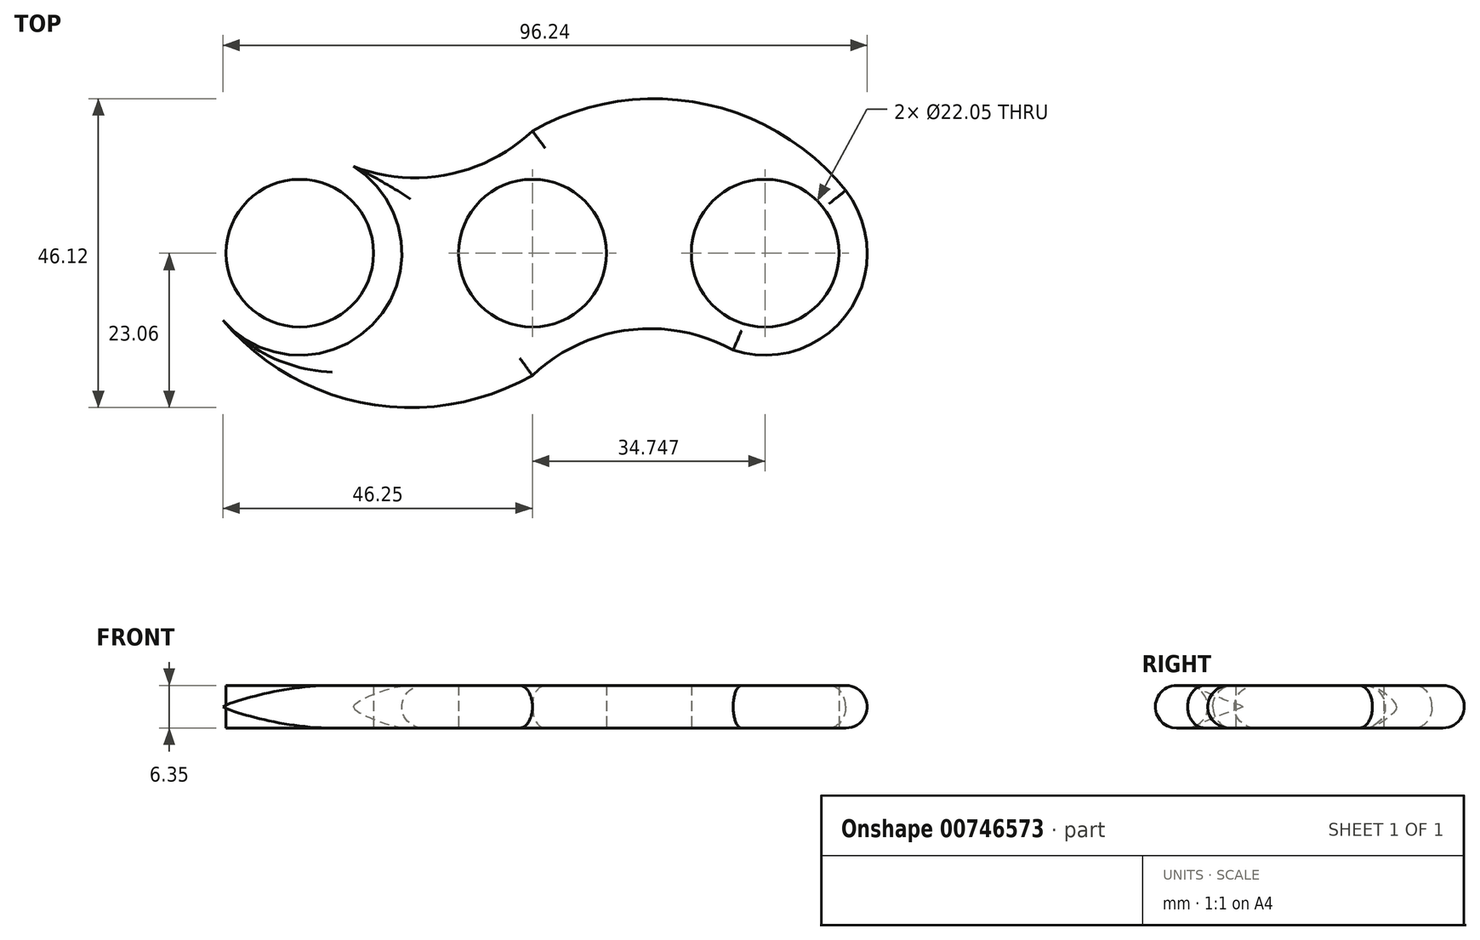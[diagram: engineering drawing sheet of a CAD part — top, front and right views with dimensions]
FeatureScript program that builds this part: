
annotation { "Feature Type Name" : "Feature", "Feature Type Description" : "" }
export const myFeature = defineFeature(function(context is Context, id is Id, definition is map)
    precondition{}
    {
        {
            var Q0;
            Q0=qCreatedBy(makeId("Top.planeOp"),FACE);
            var sketch = newSketch(context, id + "F0", { "sketchPlane" : qUnion([Q0])});
            skCircle(sketch, "E0", {"center": v(0, 0) * mm, "radius": 11.02 * mm});
            skCircle(sketch, "E1", {"center": v(34.75, 0) * mm, "radius": 11.02 * mm});
            skCircle(sketch, "E2.MirrorC", {"center": v(-34.75, 0) * mm, "radius": 11.02 * mm});
            skCircle(sketch, "E3", {"center": v(-34.75, 0) * mm, "radius": 15.24 * mm});
            skCircle(sketch, "E4.MirrorC", {"center": v(34.75, 0) * mm, "radius": 15.24 * mm});
            skArc(sketch, "E5", {"start": v(-29.97, 14.47) * mm, "mid": v(-14.37, 11.47) * mm, "end": v(0, 18.25) * mm});
            skArc(sketch, "E6", {"start": v(46.78, 9.36) * mm, "mid": v(25.03, 22.42) * mm, "end": v(0, 18.25) * mm});
            skArc(sketch, "E7.1.0", {"start": v(29.97, -14.47) * mm, "mid": v(14.37, -11.47) * mm, "end": v(0, -18.25) * mm});
            skArc(sketch, "E7.1.1", {"start": v(-46.78, -9.36) * mm, "mid": v(-25.03, -22.42) * mm, "end": v(0, -18.25) * mm});
            skSolve(sketch);
        }
        {
            var Q0;
            Q0=makeQuery(id+"F0.imprint","IMPRINT",FACE,{"disambiguationData":[TD([[makeQuery(id+"F0.imprint","IMPRINT",EDGE,{"derivedFrom":sQuery(id+"F0.wireOp",EDGE,"E2.MirrorC")}),1.0]])]});
            var Q1;
            Q1=makeQuery(id+"F0.imprint","IMPRINT",FACE,{"disambiguationData":[TD([[makeQuery(id+"F0.imprint","IMPRINT",EDGE,{"derivedFrom":sQuery(id+"F0.wireOp",EDGE,"E0")}),-1.0]])]});
            var Q2;
            Q2=makeQuery(id+"F0.imprint","IMPRINT",FACE,{"disambiguationData":[TD([[makeQuery(id+"F0.imprint","IMPRINT",EDGE,{"derivedFrom":sQuery(id+"F0.wireOp",EDGE,"E1")}),-1.0]])]});
            extrude(context, id + "F1", {"entities" : qUnion([Q0, Q1, Q2]), "depth" : 6.35 * mm, "offsetDistance" : 25.4 * mm});
        }
        {
            var Q0;
            Q0=makeQuery(id+"F1.opExtrude","CAP_EDGE",EDGE,{"disambiguationData":[OSD([sQuery(id+"F0.wireOp",EDGE,"E5")])],"isStart":false});
            var Q1;
            Q1=makeQuery(id+"F1.opExtrude","CAP_EDGE",EDGE,{"disambiguationData":[OSD([sQuery(id+"F0.wireOp",EDGE,"E3")])],"isStart":false});
            var Q2;
            Q2=makeQuery(id+"F1.opExtrude","CAP_EDGE",EDGE,{"disambiguationData":[OSD([sQuery(id+"F0.wireOp",EDGE,"E7.1.1")])],"isStart":false});
            var Q3;
            Q3=makeQuery(id+"F1.opExtrude","CAP_EDGE",EDGE,{"disambiguationData":[OSD([sQuery(id+"F0.wireOp",EDGE,"E7.1.0")])],"isStart":false});
            var Q4;
            Q4=makeQuery(id+"F1.opExtrude","CAP_EDGE",EDGE,{"disambiguationData":[OSD([sQuery(id+"F0.wireOp",EDGE,"E6")])],"isStart":false});
            var Q5;
            Q5=makeQuery(id+"F1.opExtrude","CAP_EDGE",EDGE,{"disambiguationData":[OSD([sQuery(id+"F0.wireOp",EDGE,"E4.MirrorC")])],"isStart":false});
            fillet(context, id + "F2", {"entities" : qUnion([Q0, Q1, Q2, Q3, Q4, Q5]), "radius" : 3.17 * mm, "tangentPropagation" : true, "allowEdgeOverflow" : false});
        }
        {
            var Q0;
            Q0=makeQuery(id+"F1.opExtrude","CAP_EDGE",EDGE,{"disambiguationData":[OSD([sQuery(id+"F0.wireOp",EDGE,"E7.1.1")])],"isStart":true});
            var Q1;
            Q1=makeQuery(id+"F1.opExtrude","CAP_EDGE",EDGE,{"disambiguationData":[OSD([sQuery(id+"F0.wireOp",EDGE,"E6")])],"isStart":true});
            var Q2;
            Q2=makeQuery(id+"F1.opExtrude","CAP_EDGE",EDGE,{"disambiguationData":[OSD([sQuery(id+"F0.wireOp",EDGE,"E5")])],"isStart":true});
            var Q3;
            Q3=makeQuery(id+"F1.opExtrude","CAP_EDGE",EDGE,{"disambiguationData":[OSD([sQuery(id+"F0.wireOp",EDGE,"E7.1.0")])],"isStart":true});
            var Q4;
            Q4=makeQuery(id+"F1.opExtrude","CAP_EDGE",EDGE,{"disambiguationData":[OSD([sQuery(id+"F0.wireOp",EDGE,"E4.MirrorC")])],"isStart":true});
            var Q5;
            Q5=makeQuery(id+"F1.opExtrude","CAP_EDGE",EDGE,{"disambiguationData":[OSD([sQuery(id+"F0.wireOp",EDGE,"E3")])],"isStart":true});
            fillet(context, id + "F3", {"entities" : qUnion([Q0, Q1, Q2, Q3, Q4, Q5]), "radius" : 3.17 * mm, "tangentPropagation" : true, "allowEdgeOverflow" : false});
        }
    });
